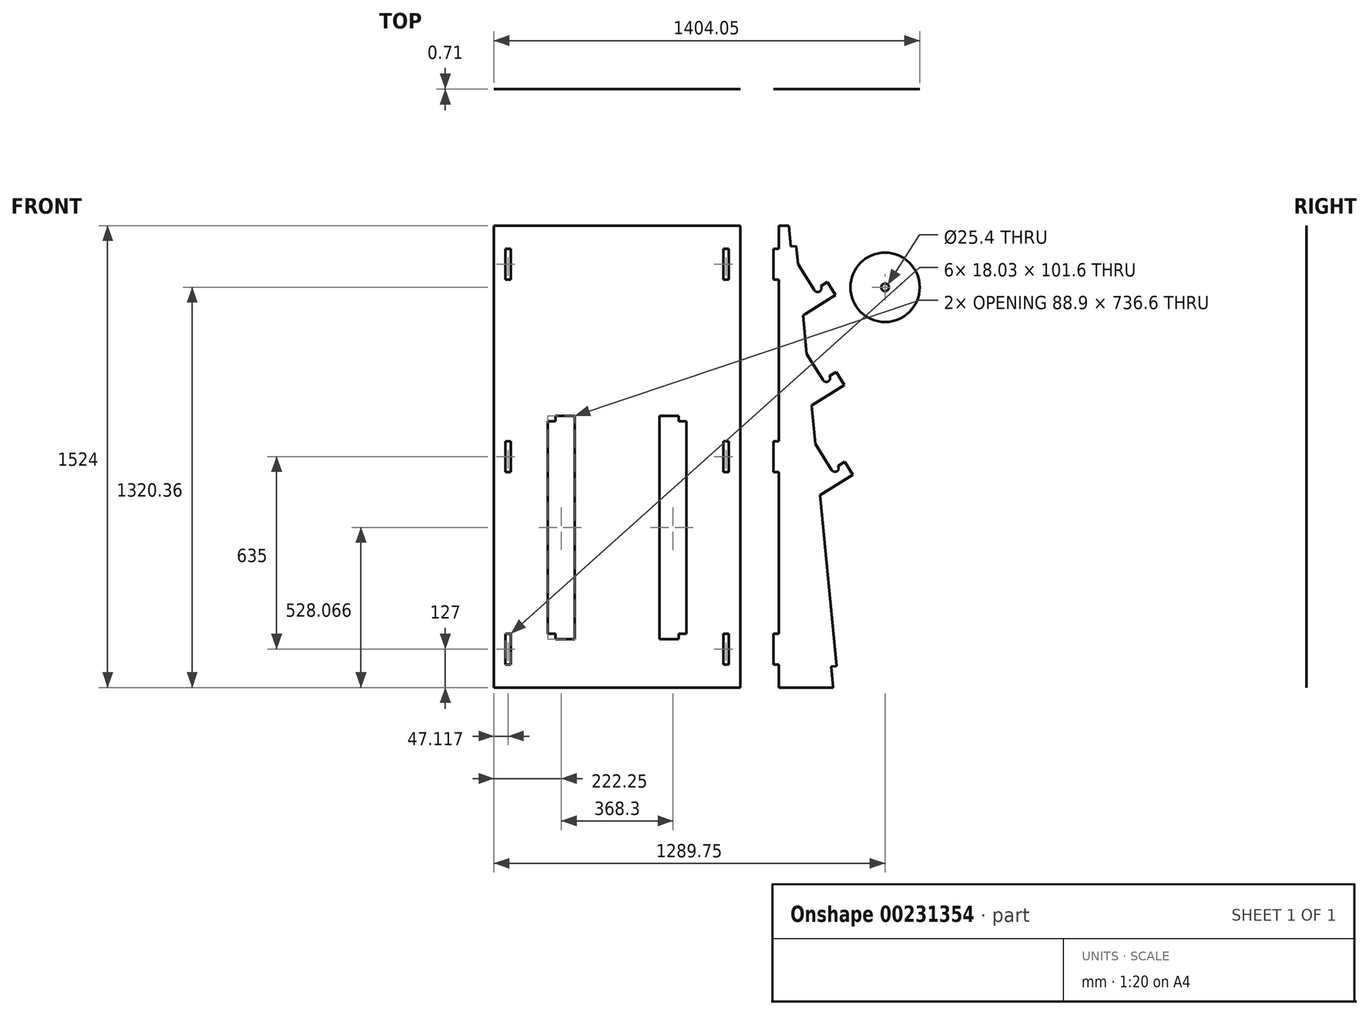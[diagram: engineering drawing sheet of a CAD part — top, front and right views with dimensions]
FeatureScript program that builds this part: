
annotation { "Feature Type Name" : "Feature", "Feature Type Description" : "" }
export const myFeature = defineFeature(function(context is Context, id is Id, definition is map)
    precondition{}
    {
        {
            assignVariable(context, id + "F0", {"name" : "thick", "anyValue" : .71});
        }
        {
            var Q0;
            Q0=qCreatedBy(makeId("Front.planeOp"),FACE);
            var sketch = newSketch(context, id + "F1", { "sketchPlane" : qUnion([Q0])});
            skLineSegment(sketch, "E0.bottom", {"start": v(-406.4, 762) * mm, "end": v(406.4, 762) * mm});
            skLineSegment(sketch, "E0.top", {"start": v(-406.4, -762) * mm, "end": v(406.4, -762) * mm});
            skLineSegment(sketch, "E0.left", {"start": v(-406.4, 762) * mm, "end": v(-406.4, -762) * mm});
            skLineSegment(sketch, "E0.right", {"start": v(406.4, 762) * mm, "end": v(406.4, -762) * mm});
            skPoint(sketch, "E0.middle", {"position": v(0, 0) * mm});
            skLineSegment(sketch, "E1", {"start": v(533.4, 762) * mm, "end": v(533.4, -762) * mm});
            skLineSegment(sketch, "E2", {"start": v(533.4, -762) * mm, "end": v(730.25, -762) * mm});
            skLineSegment(sketch, "E3", {"start": v(730.25, -762) * mm, "end": v(590.7, 694.19) * mm});
            skLineSegment(sketch, "E4", {"start": v(566.08, 762) * mm, "end": v(533.4, 762) * mm});
            skCircle(sketch, "E5", {"center": v(883.35, 558.36) * mm, "radius": 114.3 * mm});
            skLineSegment(sketch, "E6", {"start": v(607.2, 521.93) * mm, "end": v(650.27, 548.88) * mm});
            skLineSegment(sketch, "E7", {"start": v(693.33, 575.82) * mm, "end": v(720.28, 532.76) * mm});
            skLineSegment(sketch, "E8", {"start": v(720.28, 532.76) * mm, "end": v(612.63, 465.39) * mm});
            skCircle(sketch, "E9", {"center": v(883.35, 558.36) * mm, "radius": 12.7 * mm});
            skLineSegment(sketch, "E10", {"start": v(650.27, 548.88) * mm, "end": v(596.37, 635) * mm});
            skArc(sketch, "E11", {"start": v(650.27, 548.88) * mm, "mid": v(667.77, 544.85) * mm, "end": v(671.8, 562.35) * mm});
            skLineSegment(sketch, "E12.trimOffspring", {"start": v(671.8, 562.35) * mm, "end": v(693.33, 575.82) * mm});
            skLineSegment(sketch, "E13", {"start": v(635.63, 225.31) * mm, "end": v(678.7, 252.26) * mm});
            skLineSegment(sketch, "E14", {"start": v(721.76, 279.21) * mm, "end": v(748.7, 236.15) * mm});
            skLineSegment(sketch, "E15", {"start": v(748.7, 236.15) * mm, "end": v(641.05, 168.78) * mm});
            skLineSegment(sketch, "E16", {"start": v(678.7, 252.26) * mm, "end": v(624.8, 338.39) * mm});
            skArc(sketch, "E17", {"start": v(678.7, 252.26) * mm, "mid": v(696.2, 248.24) * mm, "end": v(700.23, 265.74) * mm});
            skLineSegment(sketch, "E18.trimOffspring", {"start": v(700.23, 265.74) * mm, "end": v(721.76, 279.21) * mm});
            skLineSegment(sketch, "E19", {"start": v(664.06, -71.3) * mm, "end": v(707.12, -44.35) * mm});
            skLineSegment(sketch, "E20", {"start": v(750.18, -17.4) * mm, "end": v(777.13, -60.46) * mm});
            skLineSegment(sketch, "E21", {"start": v(777.13, -60.46) * mm, "end": v(669.48, -127.83) * mm});
            skLineSegment(sketch, "E22", {"start": v(707.12, -44.35) * mm, "end": v(653.22, 41.78) * mm});
            skArc(sketch, "E23", {"start": v(707.12, -44.35) * mm, "mid": v(724.62, -48.38) * mm, "end": v(728.65, -30.87) * mm});
            skLineSegment(sketch, "E24.trimOffspring", {"start": v(728.65, -30.87) * mm, "end": v(750.18, -17.4) * mm});
            skLineSegment(sketch, "E25.bottom", {"start": v(533.4, 685.8) * mm, "end": v(515.37, 685.8) * mm});
            skLineSegment(sketch, "E25.top", {"start": v(533.4, 584.2) * mm, "end": v(515.37, 584.2) * mm});
            skLineSegment(sketch, "E25.left", {"start": v(533.4, 685.8) * mm, "end": v(533.4, 584.2) * mm});
            skLineSegment(sketch, "E25.right", {"start": v(515.37, 685.8) * mm, "end": v(515.37, 584.2) * mm});
            skLineSegment(sketch, "E26.bottom", {"start": v(-350.27, 685.8) * mm, "end": v(-368.3, 685.8) * mm});
            skLineSegment(sketch, "E26.top", {"start": v(-350.27, 584.2) * mm, "end": v(-368.3, 584.2) * mm});
            skLineSegment(sketch, "E26.left", {"start": v(-350.27, 685.8) * mm, "end": v(-350.27, 584.2) * mm});
            skLineSegment(sketch, "E26.right", {"start": v(-368.3, 685.8) * mm, "end": v(-368.3, 584.2) * mm});
            skLineSegment(sketch, "E27", {"start": v(-406.4, 0) * mm, "end": v(406.4, 0) * mm, "construction": true});
            skLineSegment(sketch, "E28.MirrorCS", {"start": v(-350.27, -584.2) * mm, "end": v(-368.3, -584.2) * mm});
            skLineSegment(sketch, "E29.MirrorCS", {"start": v(533.4, -685.8) * mm, "end": v(515.37, -685.8) * mm});
            skLineSegment(sketch, "E30.MirrorCS", {"start": v(533.4, -584.2) * mm, "end": v(515.37, -584.2) * mm});
            skLineSegment(sketch, "E31.MirrorCS", {"start": v(-350.27, -685.8) * mm, "end": v(-368.3, -685.8) * mm});
            skLineSegment(sketch, "E32.MirrorCS", {"start": v(-368.3, -685.8) * mm, "end": v(-368.3, -584.2) * mm});
            skLineSegment(sketch, "E33.MirrorCS", {"start": v(-350.27, -685.8) * mm, "end": v(-350.27, -584.2) * mm});
            skLineSegment(sketch, "E34.MirrorCS", {"start": v(515.37, -685.8) * mm, "end": v(515.37, -584.2) * mm});
            skLineSegment(sketch, "E35.MirrorCS", {"start": v(533.4, -685.8) * mm, "end": v(533.4, -584.2) * mm});
            skLineSegment(sketch, "E36.bottom", {"start": v(-368.3, 50.8) * mm, "end": v(-350.27, 50.8) * mm});
            skLineSegment(sketch, "E36.top", {"start": v(-368.3, -50.8) * mm, "end": v(-350.27, -50.8) * mm});
            skLineSegment(sketch, "E36.left", {"start": v(-368.3, 50.8) * mm, "end": v(-368.3, -50.8) * mm});
            skLineSegment(sketch, "E36.right", {"start": v(-350.27, 50.8) * mm, "end": v(-350.27, -50.8) * mm});
            skPoint(sketch, "E37", {"position": v(-368.3, 0) * mm});
            skLineSegment(sketch, "E38", {"start": v(0, 762) * mm, "end": v(0, -762) * mm, "construction": true});
            skLineSegment(sketch, "E39.MirrorCS", {"start": v(350.27, 584.2) * mm, "end": v(368.3, 584.2) * mm});
            skLineSegment(sketch, "E40.MirrorCS", {"start": v(368.3, 50.8) * mm, "end": v(350.27, 50.8) * mm});
            skLineSegment(sketch, "E41.MirrorCS", {"start": v(350.27, -584.2) * mm, "end": v(368.3, -584.2) * mm});
            skLineSegment(sketch, "E42.MirrorCS", {"start": v(350.27, 685.8) * mm, "end": v(368.3, 685.8) * mm});
            skLineSegment(sketch, "E43.MirrorCS", {"start": v(368.3, -50.8) * mm, "end": v(350.27, -50.8) * mm});
            skLineSegment(sketch, "E44.MirrorCS", {"start": v(350.27, -685.8) * mm, "end": v(368.3, -685.8) * mm});
            skLineSegment(sketch, "E45.MirrorCS", {"start": v(368.3, 50.8) * mm, "end": v(368.3, -50.8) * mm});
            skLineSegment(sketch, "E46.MirrorCS", {"start": v(350.27, 50.8) * mm, "end": v(350.27, -50.8) * mm});
            skLineSegment(sketch, "E47.MirrorCS", {"start": v(350.27, 685.8) * mm, "end": v(350.27, 584.2) * mm});
            skLineSegment(sketch, "E48.MirrorCS", {"start": v(368.3, -685.8) * mm, "end": v(368.3, -584.2) * mm});
            skLineSegment(sketch, "E49.MirrorCS", {"start": v(350.27, -685.8) * mm, "end": v(350.27, -584.2) * mm});
            skLineSegment(sketch, "E50.MirrorCS", {"start": v(368.3, 685.8) * mm, "end": v(368.3, 584.2) * mm});
            skLineSegment(sketch, "E51.MirrorCS", {"start": v(406.4, 762) * mm, "end": v(-406.4, 762) * mm});
            skPoint(sketch, "E52.MirrorP", {"position": v(368.3, 0) * mm});
            skLineSegment(sketch, "E53.bottom", {"start": v(533.4, 50.8) * mm, "end": v(515.37, 50.8) * mm});
            skLineSegment(sketch, "E53.top", {"start": v(533.4, -50.8) * mm, "end": v(515.37, -50.8) * mm});
            skLineSegment(sketch, "E53.left", {"start": v(533.4, 50.8) * mm, "end": v(533.4, -50.8) * mm});
            skLineSegment(sketch, "E53.right", {"start": v(515.37, 50.8) * mm, "end": v(515.37, -50.8) * mm});
            skLineSegment(sketch, "E54", {"start": v(590.7, 694.19) * mm, "end": v(572.75, 692.47) * mm});
            skLineSegment(sketch, "E55", {"start": v(572.75, 692.47) * mm, "end": v(566.08, 762) * mm});
            skPoint(sketch, "E56.orphan", {"position": v(584.2, 762) * mm});
            skLineSegment(sketch, "E57", {"start": v(712.13, -762) * mm, "end": v(705.47, -692.47) * mm});
            skLineSegment(sketch, "E58", {"start": v(705.47, -692.47) * mm, "end": v(723.42, -690.75) * mm});
            skLineSegment(sketch, "E59.bottom", {"start": v(-228.6, -584.2) * mm, "end": v(-139.7, -584.2) * mm});
            skLineSegment(sketch, "E59.top", {"start": v(-228.6, 116.33) * mm, "end": v(-139.7, 116.33) * mm});
            skLineSegment(sketch, "E59.left", {"start": v(-228.6, -584.2) * mm, "end": v(-228.6, 116.33) * mm});
            skLineSegment(sketch, "E59.right", {"start": v(-139.7, -584.2) * mm, "end": v(-139.7, 116.33) * mm});
            skLineSegment(sketch, "E60", {"start": v(-139.7, -584.2) * mm, "end": v(-139.7, -602.23) * mm});
            skLineSegment(sketch, "E61", {"start": v(-139.7, -602.23) * mm, "end": v(-203.2, -602.23) * mm});
            skLineSegment(sketch, "E62", {"start": v(-203.2, -602.23) * mm, "end": v(-203.2, -584.2) * mm});
            skLineSegment(sketch, "E63", {"start": v(-139.7, 116.33) * mm, "end": v(-139.7, 134.37) * mm});
            skLineSegment(sketch, "E64", {"start": v(-139.7, 134.37) * mm, "end": v(-203.2, 134.37) * mm});
            skLineSegment(sketch, "E65", {"start": v(-203.2, 134.37) * mm, "end": v(-203.2, 116.33) * mm});
            skLineSegment(sketch, "E66.MirrorCS", {"start": v(139.7, -584.2) * mm, "end": v(139.7, -602.23) * mm});
            skLineSegment(sketch, "E67.MirrorCS", {"start": v(139.7, 116.33) * mm, "end": v(139.7, 134.37) * mm});
            skLineSegment(sketch, "E68.MirrorCS", {"start": v(203.2, -602.23) * mm, "end": v(203.2, -584.2) * mm});
            skLineSegment(sketch, "E69.MirrorCS", {"start": v(203.2, 134.37) * mm, "end": v(203.2, 116.33) * mm});
            skLineSegment(sketch, "E70.MirrorCS", {"start": v(139.7, -602.23) * mm, "end": v(203.2, -602.23) * mm});
            skLineSegment(sketch, "E71.MirrorCS", {"start": v(139.7, 134.37) * mm, "end": v(203.2, 134.37) * mm});
            skLineSegment(sketch, "E72.MirrorCS", {"start": v(228.6, -584.2) * mm, "end": v(139.7, -584.2) * mm});
            skLineSegment(sketch, "E73.MirrorCS", {"start": v(228.6, 116.33) * mm, "end": v(139.7, 116.33) * mm});
            skLineSegment(sketch, "E74.MirrorCS", {"start": v(228.6, -584.2) * mm, "end": v(228.6, 116.33) * mm});
            skLineSegment(sketch, "E75.MirrorCS", {"start": v(139.7, -584.2) * mm, "end": v(139.7, 116.33) * mm});
            skSolve(sketch);
        }
        {
            var Q0;
            Q0=makeQuery(id+"F1.imprint","IMPRINT",FACE,{"disambiguationData":[TD([[makeQuery(id+"F1.imprint","IMPRINT",EDGE,{"derivedFrom":sQuery(id+"F1.wireOp",EDGE,"E0.top")}),1.0]])]});
            var Q1;
            Q1=makeQuery(id+"F1.imprint","IMPRINT",FACE,{"disambiguationData":[TD([[makeQuery(id+"F1.imprint","IMPRINT",EDGE,{"derivedFrom":sQuery(id+"F1.wireOp",EDGE,"E29.MirrorCS")}),-1.0]])]});
            var Q2;
            Q2=makeQuery(id+"F1.imprint","IMPRINT",FACE,{"disambiguationData":[TD([[makeQuery(id+"F1.imprint","IMPRINT",EDGE,{"derivedFrom":sQuery(id+"F1.wireOp",EDGE,"E53.bottom")}),1.0]])]});
            var Q3;
            Q3=makeQuery(id+"F1.imprint","IMPRINT",FACE,{"disambiguationData":[TD([[makeQuery(id+"F1.imprint","IMPRINT",EDGE,{"derivedFrom":sQuery(id+"F1.wireOp",EDGE,"E25.bottom")}),1.0]])]});
            var Q4;
            {var subQ0=sQuery(id+"F1.wireOp",EDGE,"E6");Q4=makeQuery(id+"F1.imprint","IMPRINT",FACE,{"disambiguationData":[TD([[makeQuery(id+"F1.imprint","IMPRINT",EDGE,{"derivedFrom":subQ0}),1.0]])]});}
            var Q5;
            {var subQ1=sQuery(id+"F1.wireOp",EDGE,"E6");Q5=makeQuery(id+"F1.imprint","IMPRINT",FACE,{"disambiguationData":[TD([[makeQuery(id+"F1.imprint","IMPRINT",EDGE,{"derivedFrom":subQ1}),-1.0]])]});}
            var Q6;
            {var subQ0=sQuery(id+"F1.wireOp",EDGE,"E13");Q6=makeQuery(id+"F1.imprint","IMPRINT",FACE,{"disambiguationData":[TD([[makeQuery(id+"F1.imprint","IMPRINT",EDGE,{"derivedFrom":subQ0}),1.0]])]});}
            var Q7;
            {var subQ1=sQuery(id+"F1.wireOp",EDGE,"E13");Q7=makeQuery(id+"F1.imprint","IMPRINT",FACE,{"disambiguationData":[TD([[makeQuery(id+"F1.imprint","IMPRINT",EDGE,{"derivedFrom":subQ1}),-1.0]])]});}
            var Q8;
            {var subQ0=sQuery(id+"F1.wireOp",EDGE,"E19");Q8=makeQuery(id+"F1.imprint","IMPRINT",FACE,{"disambiguationData":[TD([[makeQuery(id+"F1.imprint","IMPRINT",EDGE,{"derivedFrom":subQ0}),1.0]])]});}
            var Q9;
            {var subQ1=sQuery(id+"F1.wireOp",EDGE,"E19");Q9=makeQuery(id+"F1.imprint","IMPRINT",FACE,{"disambiguationData":[TD([[makeQuery(id+"F1.imprint","IMPRINT",EDGE,{"derivedFrom":subQ1}),-1.0]])]});}
            var Q10;
            {var subQ13=sQuery(id+"F1.wireOp",EDGE,"E4");Q10=makeQuery(id+"F1.imprint","IMPRINT",FACE,{"disambiguationData":[TD([[makeQuery(id+"F1.imprint","IMPRINT",EDGE,{"derivedFrom":subQ13}),1.0]])]});}
            var Q11;
            Q11=makeQuery(id+"F1.imprint","IMPRINT",FACE,{"disambiguationData":[TD([[makeQuery(id+"F1.imprint","IMPRINT",EDGE,{"derivedFrom":sQuery(id+"F1.wireOp",EDGE,"E5")}),1.0]])]});
            extrude(context, id + "F2", {"entities" : qUnion([Q0, Q1, Q2, Q3, Q4, Q5, Q6, Q7, Q8, Q9, Q10, Q11]), "depth" : (getVariable(context, 'thick')) * mm});
        }
        {
            var Q0;
            {var subQ3=sQuery(id+"F1.wireOp",EDGE,"E59.left");Q0=makeQuery(id+"F1.imprint","IMPRINT",FACE,{"disambiguationData":[TD([[makeQuery(id+"F1.imprint","IMPRINT",EDGE,{"derivedFrom":subQ3}),-1.0]])]});}
            var Q1;
            {var subQ0=sQuery(id+"F1.wireOp",EDGE,"E63");Q1=makeQuery(id+"F1.imprint","IMPRINT",FACE,{"disambiguationData":[TD([[makeQuery(id+"F1.imprint","IMPRINT",EDGE,{"derivedFrom":subQ0}),1.0]])]});}
            var Q2;
            {var subQ0=sQuery(id+"F1.wireOp",EDGE,"E67.MirrorCS");Q2=makeQuery(id+"F1.imprint","IMPRINT",FACE,{"disambiguationData":[TD([[makeQuery(id+"F1.imprint","IMPRINT",EDGE,{"derivedFrom":subQ0}),-1.0]])]});}
            var Q3;
            {var subQ3=sQuery(id+"F1.wireOp",EDGE,"E74.MirrorCS");Q3=makeQuery(id+"F1.imprint","IMPRINT",FACE,{"disambiguationData":[TD([[makeQuery(id+"F1.imprint","IMPRINT",EDGE,{"derivedFrom":subQ3}),1.0]])]});}
            var Q4;
            {var subQ0=sQuery(id+"F1.wireOp",EDGE,"E66.MirrorCS");Q4=makeQuery(id+"F1.imprint","IMPRINT",FACE,{"disambiguationData":[TD([[makeQuery(id+"F1.imprint","IMPRINT",EDGE,{"derivedFrom":subQ0}),1.0]])]});}
            var Q5;
            {var subQ0=sQuery(id+"F1.wireOp",EDGE,"E60");Q5=makeQuery(id+"F1.imprint","IMPRINT",FACE,{"disambiguationData":[TD([[makeQuery(id+"F1.imprint","IMPRINT",EDGE,{"derivedFrom":subQ0}),-1.0]])]});}
            extrude(context, id + "F3", {"entities" : qUnion([Q0, Q1, Q2, Q3, Q4, Q5]), "depth" : (getVariable(context, 'thick')) * mm});
        }
    });
